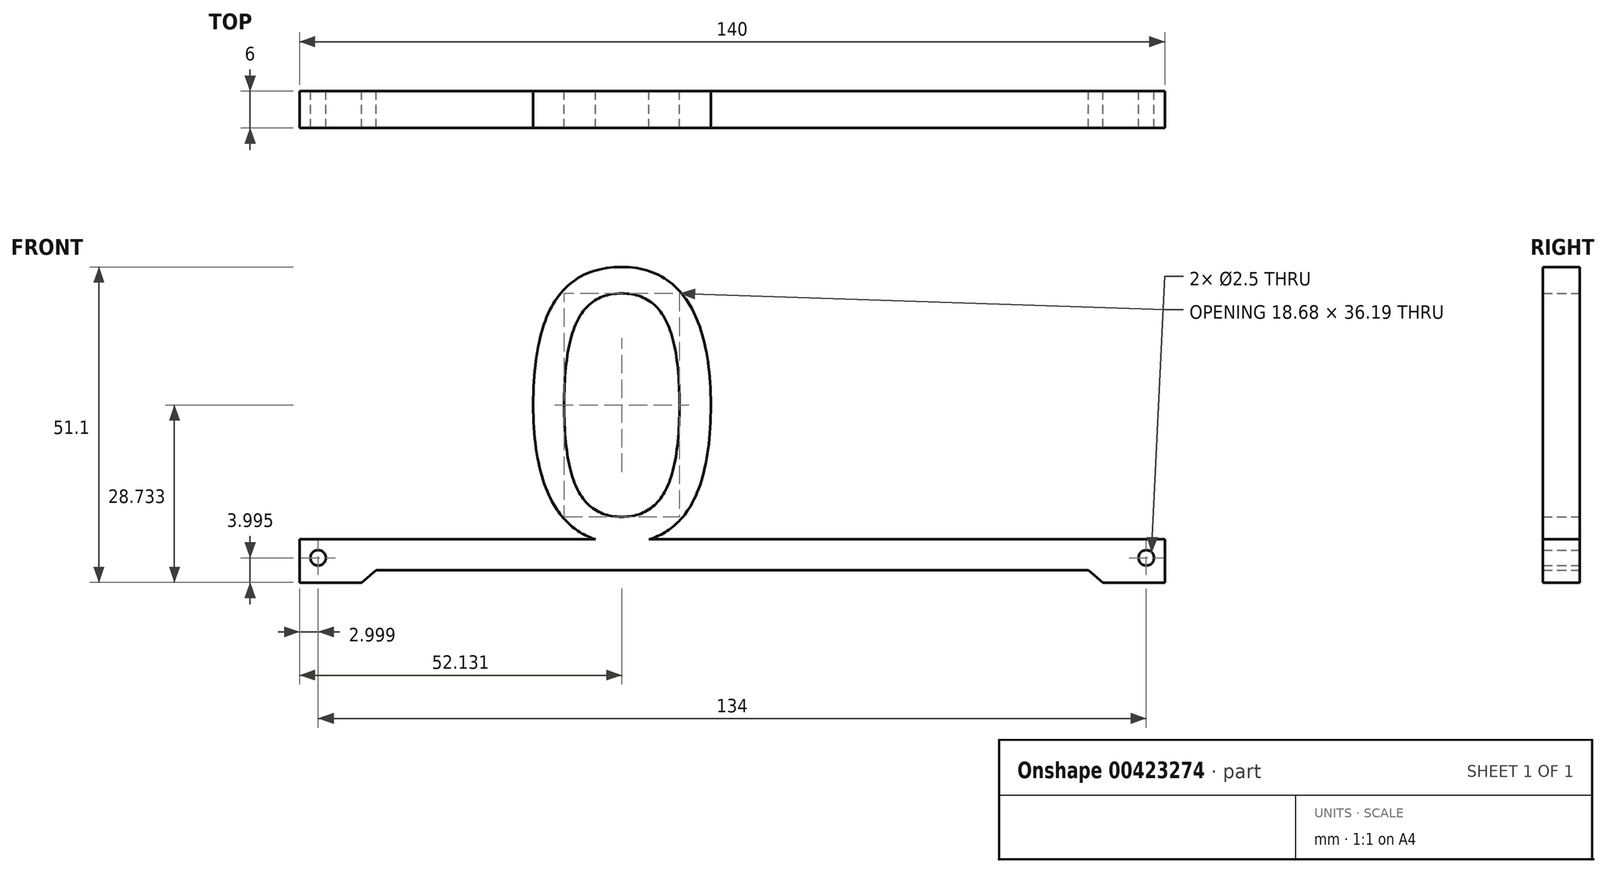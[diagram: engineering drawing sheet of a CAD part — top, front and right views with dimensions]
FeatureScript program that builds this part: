
annotation { "Feature Type Name" : "Feature", "Feature Type Description" : "" }
export const myFeature = defineFeature(function(context is Context, id is Id, definition is map)
    precondition{}
    {
        {
            var Q0;
            Q0=qCreatedBy(makeId("Front.planeOp"),FACE);
            var sketch = newSketch(context, id + "F0", { "sketchPlane" : qUnion([Q0])});
            skText(sketch, "E0", { "text": "2017", "fontName": "OpenSans-Regular.ttf"});
            skLineSegment(sketch, "E1.bottom", {"start": v(-94.7, 0.1) * mm, "end": v(45.3, 0.1) * mm});
            skLineSegment(sketch, "E1.top", {"start": v(-94.7, -6.9) * mm, "end": v(-84.7, -6.9) * mm});
            skLineSegment(sketch, "E1.left", {"start": v(-94.7, 0.1) * mm, "end": v(-94.7, -6.9) * mm});
            skLineSegment(sketch, "E1.right", {"start": v(45.3, 0.1) * mm, "end": v(45.3, -6.9) * mm});
            skPoint(sketch, "E2", {"position": v(-91.7, -2.9) * mm});
            skPoint(sketch, "E3", {"position": v(42.3, -2.9) * mm});
            skLineSegment(sketch, "E4", {"start": v(-84.7, -6.9) * mm, "end": v(-82.3, -4.9) * mm});
            skLineSegment(sketch, "E5", {"start": v(-82.3, -4.9) * mm, "end": v(32.93, -4.9) * mm});
            skLineSegment(sketch, "E6", {"start": v(32.93, -4.9) * mm, "end": v(35.3, -6.9) * mm});
            skLineSegment(sketch, "E7.trimOffspring", {"start": v(35.3, -6.9) * mm, "end": v(45.3, -6.9) * mm});
            const initialGuessF0  = {"E0": [-0.0947, 0.0001, 1, 0, 0.0438]};
            skSetInitialGuess(sketch, initialGuessF0);
            skSolve(sketch);
        }
        {
            var Q0;
            {var subQ14=sQuery(id+"F0.wireOp",EDGE,"E1.left");Q0=makeQuery(id+"F0.imprint","IMPRINT",FACE,{"disambiguationData":[TD([[makeQuery(id+"F0.imprint","IMPRINT",EDGE,{"derivedFrom":subQ14}),1.0]])]});}
            var Q1;
            {var subQ0=sQuery(id+"F0.wireOp",EDGE,"E0.sketch_text.stroke-20");Q1=makeQuery(id+"F0.imprint","IMPRINT",FACE,{"disambiguationData":[TD([[makeQuery(id+"F0.imprint","IMPRINT",EDGE,{"derivedFrom":subQ0}),-1.0]])]});}
            var Q2;
            {var subQ1=sQuery(id+"F0.wireOp",EDGE,"E0.sketch_text.stroke-1");Q2=makeQuery(id+"F0.imprint","IMPRINT",FACE,{"disambiguationData":[TD([[makeQuery(id+"F0.imprint","IMPRINT",EDGE,{"derivedFrom":subQ1}),-1.0]])]});}
            var Q3;
            {var subQ0=sQuery(id+"F0.wireOp",EDGE,"E0.sketch_text.stroke-37");Q3=makeQuery(id+"F0.imprint","IMPRINT",FACE,{"disambiguationData":[TD([[makeQuery(id+"F0.imprint","IMPRINT",EDGE,{"derivedFrom":subQ0}),-1.0]])]});}
            var Q4;
            {var subQ1=sQuery(id+"F0.wireOp",EDGE,"E0.sketch_text.stroke-45");Q4=makeQuery(id+"F0.imprint","IMPRINT",FACE,{"disambiguationData":[TD([[makeQuery(id+"F0.imprint","IMPRINT",EDGE,{"derivedFrom":subQ1}),-1.0]])]});}
            var Q5;
            {var subQ0=sQuery(id+"F0.wireOp",EDGE,"E0.sketch_text.stroke-22");var subQ1=sQuery(id+"F0.wireOp",EDGE,"E0.sketch_text.stroke-21");var subQ2=makeQuery(id+"F0.imprint","INTERSECT",VERTEX,{"derivedFrom":[subQ1,subQ0]});Q5=makeQuery(id+"F0.imprint","IMPRINT",FACE,{"disambiguationData":[TD([[makeQuery(id+"F0.imprint","IMPRINT",EDGE,{"disambiguationData":[TD([[subQ2,1.0]])],"derivedFrom":subQ1}),-1.0]])]});}
            extrude(context, id + "F1", {"entities" : qUnion([Q0, Q1, Q2, Q3, Q4, Q5]), "depth" : 6 * mm});
        }
        {
            var Q0;
            Q0=sQuery(id+"F0.wireOp",VERTEX,"E2");
            var Q1;
            Q1=sQuery(id+"F0.wireOp",VERTEX,"E3");
            var Q2;
            Q2=makeQuery(id+"F1.opExtrude","SWEPT_BODY",BODY,{"disambiguationData":[OSD([sQuery(id+"F0.wireOp",EDGE,"E0.sketch_text.stroke-1"),sQuery(id+"F0.wireOp",EDGE,"E0.sketch_text.stroke-2"),sQuery(id+"F0.wireOp",EDGE,"E0.sketch_text.stroke-3"),sQuery(id+"F0.wireOp",EDGE,"E0.sketch_text.stroke-4"),sQuery(id+"F0.wireOp",EDGE,"E0.sketch_text.stroke-5"),sQuery(id+"F0.wireOp",EDGE,"E0.sketch_text.stroke-6"),sQuery(id+"F0.wireOp",EDGE,"E0.sketch_text.stroke-7"),sQuery(id+"F0.wireOp",EDGE,"E0.sketch_text.stroke-8"),sQuery(id+"F0.wireOp",EDGE,"E0.sketch_text.stroke-9"),sQuery(id+"F0.wireOp",EDGE,"E0.sketch_text.stroke-10"),sQuery(id+"F0.wireOp",EDGE,"E0.sketch_text.stroke-11"),sQuery(id+"F0.wireOp",EDGE,"E0.sketch_text.stroke-12"),sQuery(id+"F0.wireOp",EDGE,"E0.sketch_text.stroke-13"),sQuery(id+"F0.wireOp",EDGE,"E0.sketch_text.stroke-14"),sQuery(id+"F0.wireOp",EDGE,"E0.sketch_text.stroke-15"),sQuery(id+"F0.wireOp",EDGE,"E0.sketch_text.stroke-16"),sQuery(id+"F0.wireOp",EDGE,"E0.sketch_text.stroke-17"),sQuery(id+"F0.wireOp",EDGE,"E0.sketch_text.stroke-18"),sQuery(id+"F0.wireOp",EDGE,"E0.sketch_text.stroke-19"),sQuery(id+"F0.wireOp",EDGE,"E0.sketch_text.stroke-20"),sQuery(id+"F0.wireOp",EDGE,"E0.sketch_text.stroke-21"),sQuery(id+"F0.wireOp",EDGE,"E0.sketch_text.stroke-22"),sQuery(id+"F0.wireOp",EDGE,"E0.sketch_text.stroke-23"),sQuery(id+"F0.wireOp",EDGE,"E0.sketch_text.stroke-24"),sQuery(id+"F0.wireOp",EDGE,"E0.sketch_text.stroke-25"),sQuery(id+"F0.wireOp",EDGE,"E0.sketch_text.stroke-26"),sQuery(id+"F0.wireOp",EDGE,"E0.sketch_text.stroke-27"),sQuery(id+"F0.wireOp",EDGE,"E0.sketch_text.stroke-28"),sQuery(id+"F0.wireOp",EDGE,"E0.sketch_text.stroke-29"),sQuery(id+"F0.wireOp",EDGE,"E0.sketch_text.stroke-30"),sQuery(id+"F0.wireOp",EDGE,"E0.sketch_text.stroke-31"),sQuery(id+"F0.wireOp",EDGE,"E0.sketch_text.stroke-32"),sQuery(id+"F0.wireOp",EDGE,"E0.sketch_text.stroke-33"),sQuery(id+"F0.wireOp",EDGE,"E0.sketch_text.stroke-34"),sQuery(id+"F0.wireOp",EDGE,"E0.sketch_text.stroke-35"),sQuery(id+"F0.wireOp",EDGE,"E0.sketch_text.stroke-37"),sQuery(id+"F0.wireOp",EDGE,"E0.sketch_text.stroke-38"),sQuery(id+"F0.wireOp",EDGE,"E0.sketch_text.stroke-39"),sQuery(id+"F0.wireOp",EDGE,"E0.sketch_text.stroke-40"),sQuery(id+"F0.wireOp",EDGE,"E0.sketch_text.stroke-41"),sQuery(id+"F0.wireOp",EDGE,"E0.sketch_text.stroke-42"),sQuery(id+"F0.wireOp",EDGE,"E0.sketch_text.stroke-43"),sQuery(id+"F0.wireOp",EDGE,"E0.sketch_text.stroke-44"),sQuery(id+"F0.wireOp",EDGE,"E0.sketch_text.stroke-45"),sQuery(id+"F0.wireOp",EDGE,"E0.sketch_text.stroke-46"),sQuery(id+"F0.wireOp",EDGE,"E0.sketch_text.stroke-47"),sQuery(id+"F0.wireOp",EDGE,"E0.sketch_text.stroke-48"),sQuery(id+"F0.wireOp",EDGE,"E0.sketch_text.stroke-49"),sQuery(id+"F0.wireOp",EDGE,"E0.sketch_text.stroke-50"),sQuery(id+"F0.wireOp",EDGE,"E1.bottom"),sQuery(id+"F0.wireOp",EDGE,"E1.top"),sQuery(id+"F0.wireOp",EDGE,"E1.left"),sQuery(id+"F0.wireOp",EDGE,"E1.right")])]});
            hole(context, id + "F2", {"style" : HoleStyle.SIMPLE, "endStyle" : HoleEndStyle.THROUGH, "oppositeDirection" : true, "standardTappedOrClearance" : lookupTablePath({ "standard" : "ISO", "engagement" : "75%", "pitch" : "0.5 mm", "size" : "M3", "type" : "Tapped" }), "standardBlindInLast" : lookupTablePath({ "standard" : "ISO", "engagement" : "75%", "pitch" : "0.5 mm", "size" : "M3", "type" : "Tapped" }), "holeDiameter" : 2.5 * mm, "showTappedDepth" : true, "isTappedThrough" : true, "tappedDepth" : 6.2 * mm, "tapClearance" : 3, "locations" : qUnion([Q0, Q1]), "scope" : qUnion([Q2]), "majorDiameter" : 3 * mm});
        }
    });
